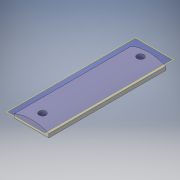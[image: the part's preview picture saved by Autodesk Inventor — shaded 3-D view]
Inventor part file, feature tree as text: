
AUTODESK INVENTOR PART (.ipt)
format: ipt  version: 2016 (Build 200138000, 138)  size: 112,640 bytes
history: native  units: in
note: dims shown in document units (in); Inventor stores cm internally (conversion verified against a paired STEP export)
features: sketch x2, extrude x1, plane x1, hole x1
ambient origin geometry x8: Origin, YZ Plane, XZ Plane, XY Plane, X Axis, Y Axis, Z Axis, Center Point
bodies: Solid1 (feature_tree)
feature tree (5):
  extrude  "Extrusion1"  Depth=0.25in
  plane  "Work Plane1"
  hole  "Hole2"  [1 undecoded]
  sketch  "Sketch1"  dims[d0=1.5in d1=0.25in]
  sketch  "Sketch5"  dims[d2=4.0in d3=0.0in d14=0.1575in d15=0.75in d16=0.2362in d17=0.1181in d18=0.5635in d19=0.3111in d20=0.8108in d4=1.0in d5=1.0in d13=1.0in]
note: 1 required parameter value undecoded (feature->parameter linkage not recoverable at this tier; creation-order binding heuristic only, values carry confidence <= 0.55)
